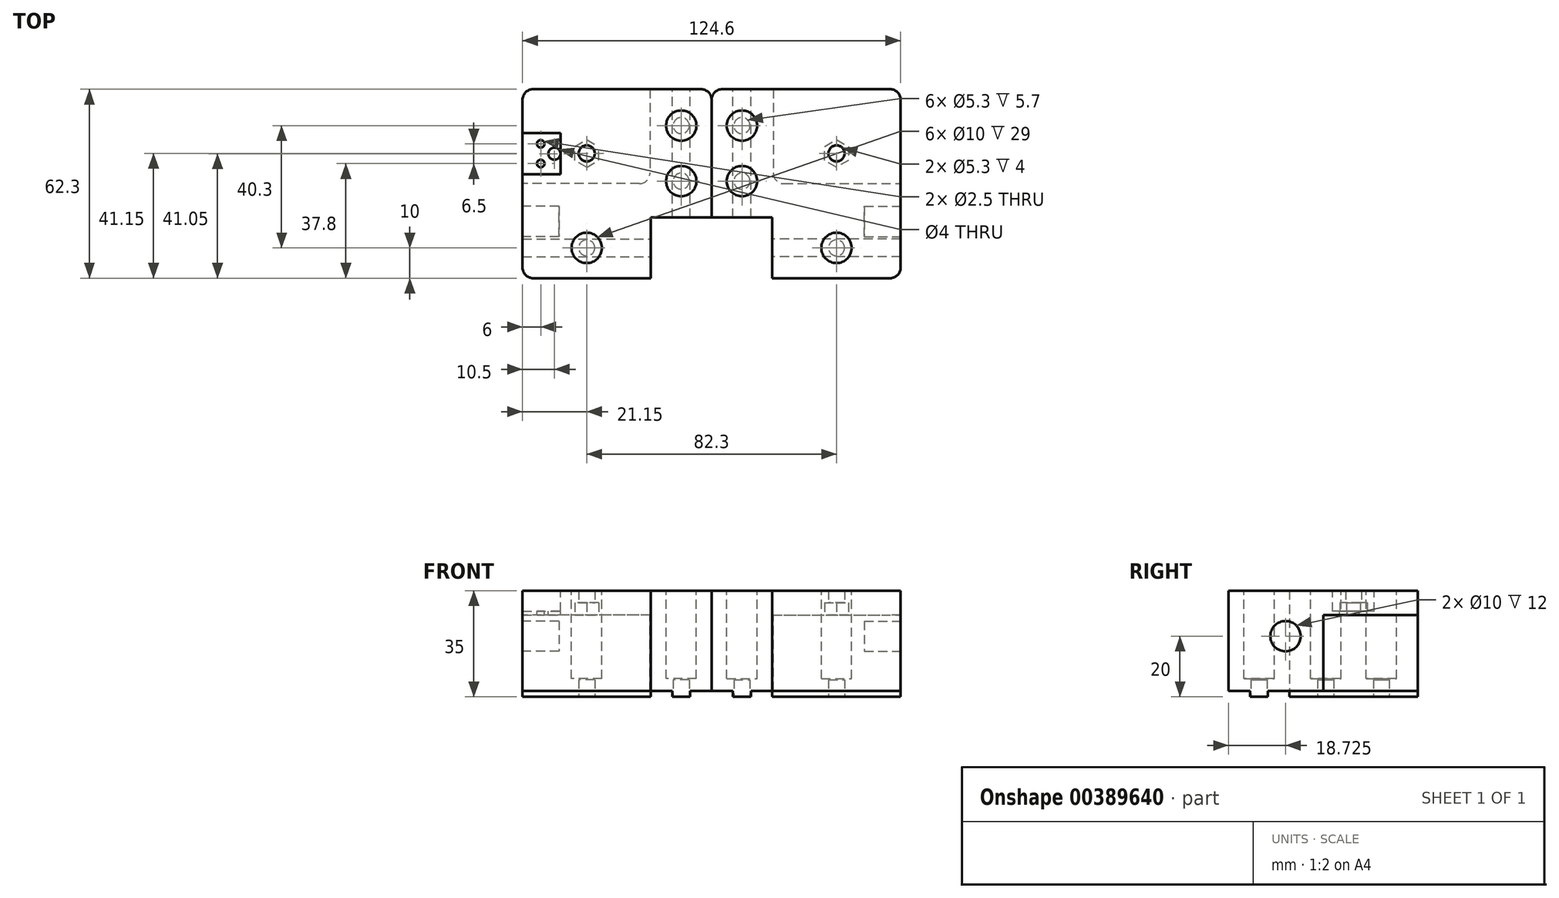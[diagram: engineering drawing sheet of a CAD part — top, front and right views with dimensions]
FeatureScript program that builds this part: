
annotation { "Feature Type Name" : "Feature", "Feature Type Description" : "" }
export const myFeature = defineFeature(function(context is Context, id is Id, definition is map)
    precondition{}
    {
        {
            var Q0;
            Q0=qCreatedBy(makeId("Top.planeOp"),FACE);
            var sketch = newSketch(context, id + "F0", { "sketchPlane" : qUnion([Q0])});
            skLineSegment(sketch, "E0.bottom", {"start": v(-21.15, 35) * mm, "end": v(41.15, 35) * mm});
            skLineSegment(sketch, "E0.top", {"start": v(-21.15, -27.3) * mm, "end": v(21.15, -27.3) * mm});
            skLineSegment(sketch, "E0.left", {"start": v(-21.15, 35) * mm, "end": v(-21.15, -27.3) * mm});
            skLineSegment(sketch, "E0.right", {"start": v(41.15, 35) * mm, "end": v(41.15, -7.3) * mm});
            skLineSegment(sketch, "E1.top", {"start": v(41.15, -7.3) * mm, "end": v(21.15, -7.3) * mm});
            skLineSegment(sketch, "E1.right", {"start": v(21.15, -27.3) * mm, "end": v(21.15, -7.3) * mm});
            skCircle(sketch, "E2", {"center": v(31.15, 23) * mm, "radius": 2.65 * mm});
            skCircle(sketch, "E3", {"center": v(31.15, 4.7) * mm, "radius": 2.65 * mm});
            skCircle(sketch, "E4", {"center": v(0, -17.3) * mm, "radius": 2.65 * mm});
            skPoint(sketch, "E4.centerSnap0", {"position": v(0, -27.3) * mm});
            skCircle(sketch, "E5", {"center": v(0, 13.85) * mm, "radius": 2.65 * mm});
            skSolve(sketch);
        }
        {
            var Q0;
            Q0=qSketchRegion(id+"F0",true);
            extrude(context, id + "F1", {"entities" : qUnion([Q0]), "depth" : 33 * mm});
        }
        {
            var Q0;
            Q0=makeQuery(id+"F1.opExtrude","SWEPT_FACE",FACE,{"disambiguationData":[OSD([sQuery(id+"F0.wireOp",EDGE,"E0.left")])]});
            var sketch = newSketch(context, id + "F2", { "sketchPlane" : qUnion([Q0])});
            skCircle(sketch, "E6", {"center": v(8.58, 18) * mm, "radius": 5 * mm});
            skSolve(sketch);
        }
        {
            var Q0;
            Q0=qSketchRegion(id+"F2",true);
            extrude(context, id + "F3", {"entities" : qUnion([Q0]), "operationType" : NewBodyOperationType.REMOVE, "oppositeDirection" : true, "depth" : 12 * mm});
        }
        {
            var Q0;
            Q0=makeQuery(id+"F1.opExtrude","CAP_FACE",FACE,{"disambiguationData":[OSD([sQuery(id+"F0.wireOp",EDGE,"E0.bottom"),sQuery(id+"F0.wireOp",EDGE,"E0.top"),sQuery(id+"F0.wireOp",EDGE,"E0.left"),sQuery(id+"F0.wireOp",EDGE,"E0.right"),sQuery(id+"F0.wireOp",EDGE,"E1.top"),sQuery(id+"F0.wireOp",EDGE,"E1.right"),sQuery(id+"F0.wireOp",EDGE,"E2"),sQuery(id+"F0.wireOp",EDGE,"E3"),sQuery(id+"F0.wireOp",EDGE,"YSbFCtBf-OZUa-blBg-jqSk-ddDIdjAn90QF"),sQuery(id+"F0.wireOp",EDGE,"E4"),sQuery(id+"F0.wireOp",EDGE,"E5")])],"isStart":true});
            var sketch = newSketch(context, id + "F4", { "sketchPlane" : qUnion([Q0])});
            skCircle(sketch, "E7.0", {"center": v(0, -13.85) * mm, "radius": 2.65 * mm, "construction": true});
            skCircle(sketch, "E8", {"center": v(0, -13.85) * mm, "radius": 3.95 * mm, "construction": true});
            skLineSegment(sketch, "E9", {"start": v(0, -20.58) * mm, "end": v(0, -4.16) * mm, "construction": true});
            skLineSegment(sketch, "E10", {"start": v(-6.74, -13.85) * mm, "end": v(6.1, -13.85) * mm, "construction": true});
            skLineSegment(sketch, "E11", {"start": v(-3.95, -16.13) * mm, "end": v(-3.95, -11.57) * mm});
            skLineSegment(sketch, "E12", {"start": v(-3.95, -11.57) * mm, "end": v(0, -9.29) * mm});
            skLineSegment(sketch, "E13", {"start": v(3.95, -16.13) * mm, "end": v(0, -18.41) * mm});
            skLineSegment(sketch, "E14", {"start": v(0, -18.41) * mm, "end": v(-3.95, -16.13) * mm});
            skLineSegment(sketch, "E15", {"start": v(3.95, -16.13) * mm, "end": v(3.95, -11.57) * mm});
            skLineSegment(sketch, "E16", {"start": v(3.95, -11.57) * mm, "end": v(0, -9.29) * mm});
            skSolve(sketch);
        }
        {
            var Q0;
            Q0=qSketchRegion(id+"F4",true);
            extrude(context, id + "F5", {"entities" : qUnion([Q0]), "operationType" : NewBodyOperationType.REMOVE, "oppositeDirection" : true, "depth" : 29 * mm});
        }
        {
            var Q0;
            Q0=makeQuery(id+"F1.opExtrude","CAP_FACE",FACE,{"disambiguationData":[OSD([sQuery(id+"F0.wireOp",EDGE,"E0.bottom"),sQuery(id+"F0.wireOp",EDGE,"E0.top"),sQuery(id+"F0.wireOp",EDGE,"E0.left"),sQuery(id+"F0.wireOp",EDGE,"E0.right"),sQuery(id+"F0.wireOp",EDGE,"E1.top"),sQuery(id+"F0.wireOp",EDGE,"E1.right"),sQuery(id+"F0.wireOp",EDGE,"E2"),sQuery(id+"F0.wireOp",EDGE,"E3"),sQuery(id+"F0.wireOp",EDGE,"YSbFCtBf-OZUa-blBg-jqSk-ddDIdjAn90QF"),sQuery(id+"F0.wireOp",EDGE,"E4"),sQuery(id+"F0.wireOp",EDGE,"E5")])],"isStart":false});
            var sketch = newSketch(context, id + "F6", { "sketchPlane" : qUnion([Q0])});
            skCircle(sketch, "E17.0", {"center": v(31.15, 23) * mm, "radius": 2.65 * mm, "construction": true});
            skCircle(sketch, "E18.0", {"center": v(31.15, 4.7) * mm, "radius": 2.65 * mm, "construction": true});
            skCircle(sketch, "E19.0", {"center": v(0, -17.3) * mm, "radius": 2.65 * mm, "construction": true});
            skCircle(sketch, "E20", {"center": v(31.15, 23) * mm, "radius": 5 * mm});
            skCircle(sketch, "E21", {"center": v(31.15, 4.7) * mm, "radius": 5 * mm});
            skCircle(sketch, "E22", {"center": v(0, -17.3) * mm, "radius": 5 * mm});
            skSolve(sketch);
        }
        {
            var Q0;
            Q0=qSketchRegion(id+"F6",true);
            extrude(context, id + "F7", {"entities" : qUnion([Q0]), "operationType" : NewBodyOperationType.REMOVE, "oppositeDirection" : true, "depth" : 29 * mm});
        }
        {
            var Q0;
            Q0=makeQuery(id+"F1.opExtrude","CAP_FACE",FACE,{"disambiguationData":[OSD([sQuery(id+"F0.wireOp",EDGE,"E0.bottom"),sQuery(id+"F0.wireOp",EDGE,"E0.top"),sQuery(id+"F0.wireOp",EDGE,"E0.left"),sQuery(id+"F0.wireOp",EDGE,"E0.right"),sQuery(id+"F0.wireOp",EDGE,"E1.top"),sQuery(id+"F0.wireOp",EDGE,"E1.right"),sQuery(id+"F0.wireOp",EDGE,"E2"),sQuery(id+"F0.wireOp",EDGE,"E3"),sQuery(id+"F0.wireOp",EDGE,"YSbFCtBf-OZUa-blBg-jqSk-ddDIdjAn90QF"),sQuery(id+"F0.wireOp",EDGE,"E4"),sQuery(id+"F0.wireOp",EDGE,"E5")])],"isStart":true});
            var sketch = newSketch(context, id + "F8", { "sketchPlane" : qUnion([Q0])});
            skLineSegment(sketch, "E23.bottom", {"start": v(28.2, 7.3) * mm, "end": v(34.1, 7.3) * mm});
            skLineSegment(sketch, "E23.top", {"start": v(28.2, -35) * mm, "end": v(34.1, -35) * mm});
            skLineSegment(sketch, "E23.left", {"start": v(28.2, 7.3) * mm, "end": v(28.2, -13.57) * mm});
            skLineSegment(sketch, "E23.right", {"start": v(34.1, 7.3) * mm, "end": v(34.1, -13.57) * mm});
            skCircle(sketch, "E24.0", {"center": v(31.15, -4.7) * mm, "radius": 2.65 * mm});
            skCircle(sketch, "E25.0", {"center": v(31.15, -23) * mm, "radius": 2.65 * mm});
            skLineSegment(sketch, "E26.trimOffspring", {"start": v(28.2, -13.57) * mm, "end": v(28.2, -35) * mm});
            skLineSegment(sketch, "E27.trimOffspring", {"start": v(34.1, -13.57) * mm, "end": v(34.1, -35) * mm});
            skLineSegment(sketch, "E28.bottom", {"start": v(-21.15, 20.25) * mm, "end": v(21.15, 20.25) * mm});
            skLineSegment(sketch, "E28.top", {"start": v(-21.15, 14.35) * mm, "end": v(21.15, 14.35) * mm});
            skLineSegment(sketch, "E28.left", {"start": v(-21.15, 20.25) * mm, "end": v(-21.15, 14.35) * mm});
            skLineSegment(sketch, "E28.right", {"start": v(21.15, 20.25) * mm, "end": v(21.15, 14.35) * mm});
            skCircle(sketch, "E29.0", {"center": v(0, 17.3) * mm, "radius": 2.65 * mm});
            skSolve(sketch);
        }
        {
            var Q0;
            Q0=qSketchRegion(id+"F8",true);
            extrude(context, id + "F9", {"entities" : qUnion([Q0]), "operationType" : NewBodyOperationType.ADD, "depth" : 2 * mm});
        }
        {
            var Q0;
            Q0=makeQuery(id+"F1.opExtrude","SWEPT_EDGE",EDGE,{"disambiguationData":[OSD([sQuery(id+"F0.wireOp",EDGE,"E0.top"),sQuery(id+"F0.wireOp",EDGE,"E0.left")])]});
            var Q1;
            Q1=makeQuery(id+"F1.opExtrude","SWEPT_EDGE",EDGE,{"disambiguationData":[OSD([sQuery(id+"F0.wireOp",EDGE,"E0.bottom"),sQuery(id+"F0.wireOp",EDGE,"E0.left")])]});
            var Q2;
            Q2=makeQuery(id+"F1.opExtrude","SWEPT_EDGE",EDGE,{"disambiguationData":[OSD([sQuery(id+"F0.wireOp",EDGE,"E0.bottom"),sQuery(id+"F0.wireOp",EDGE,"E0.right")])]});
            fillet(context, id + "F10", {"entities" : qUnion([Q0, Q1, Q2]), "radius" : 3.5 * mm, "tangentPropagation" : true, "allowEdgeOverflow" : false});
        }
        {
            var Q0;
            Q0=makeQuery(id+"F9.boolean.opBoolean","MERGE",FACE,{"derivedFrom":[makeQuery(id+"F1.opExtrude","SWEPT_FACE",FACE,{"disambiguationData":[OSD([sQuery(id+"F0.wireOp",EDGE,"E0.left")])]}),makeQuery(id+"F9.opExtrude","SWEPT_FACE",FACE,{"disambiguationData":[OSD([sQuery(id+"F8.wireOp",EDGE,"E28.left")])]})]});
            var sketch = newSketch(context, id + "F11", { "sketchPlane" : qUnion([Q0])});
            skPoint(sketch, "E30.oppositeSnap0", {"position": v(-3.85, 33) * mm});
            skLineSegment(sketch, "E30.bottom", {"start": v(-35, 0) * mm, "end": v(-3.85, 0) * mm});
            skLineSegment(sketch, "E30.top", {"start": v(-35, 25) * mm, "end": v(-3.85, 25) * mm});
            skLineSegment(sketch, "E30.left", {"start": v(-35, 0) * mm, "end": v(-35, 25) * mm});
            skLineSegment(sketch, "E30.right", {"start": v(-3.85, 0) * mm, "end": v(-3.85, 25) * mm});
            skSolve(sketch);
        }
        {
            var Q0;
            Q0=qSketchRegion(id+"F11",true);
            extrude(context, id + "F12", {"entities" : qUnion([Q0]), "operationType" : NewBodyOperationType.REMOVE, "oppositeDirection" : true, "depth" : 42 * mm});
        }
        {
            var Q0;
            Q0=makeQuery(id+"F12.boolean.opBoolean","COPY",EDGE,{"derivedFrom":makeQuery(id+"F12.opExtrude","CAP_EDGE",EDGE,{"disambiguationData":[OSD([sQuery(id+"F11.wireOp",EDGE,"E30.right")])],"isStart":true})});
            var Q1;
            Q1=makeQuery(id+"F12.boolean.opBoolean","COPY",EDGE,{"derivedFrom":makeQuery(id+"F12.opExtrude","CAP_EDGE",EDGE,{"disambiguationData":[OSD([sQuery(id+"F11.wireOp",EDGE,"E30.right")])],"isStart":false})});
            var Q2;
            Q2=makeQuery(id+"F12.boolean.opBoolean","COPY",EDGE,{"derivedFrom":makeQuery(id+"F12.opExtrude","CAP_EDGE",EDGE,{"disambiguationData":[OSD([sQuery(id+"F11.wireOp",EDGE,"E30.left")])],"isStart":false})});
            fillet(context, id + "F13", {"entities" : qUnion([Q0, Q1, Q2]), "radius" : 3.5 * mm, "tangentPropagation" : true, "allowEdgeOverflow" : false});
        }
        {
            var Q0;
            Q0=makeQuery(id+"F7.boolean.opBoolean","COPY",FACE,{"derivedFrom":makeQuery(id+"F7.opExtrude","CAP_FACE",FACE,{"disambiguationData":[OSD([sQuery(id+"F6.wireOp",EDGE,"E22")])],"isStart":false})});
            var sketch = newSketch(context, id + "F14", { "sketchPlane" : qUnion([Q0])});
            skCircle(sketch, "E31.0", {"center": v(0, -17.3) * mm, "radius": 2.65 * mm});
            skCircle(sketch, "E32.0", {"center": v(31.15, 4.7) * mm, "radius": 2.65 * mm});
            skCircle(sketch, "E33.0", {"center": v(31.15, 23) * mm, "radius": 2.65 * mm});
            skSolve(sketch);
        }
        {
            var Q0;
            Q0=qSketchRegion(id+"F14",true);
            extrude(context, id + "F15", {"entities" : qUnion([Q0]), "operationType" : NewBodyOperationType.ADD, "oppositeDirection" : true, "depth" : .3 * mm});
        }
        {
            var Q0;
            Q0=makeQuery(id+"F1.opExtrude","SWEPT_BODY",BODY,{"disambiguationData":[OSD([sQuery(id+"F0.wireOp",EDGE,"E0.bottom"),sQuery(id+"F0.wireOp",EDGE,"E0.top"),sQuery(id+"F0.wireOp",EDGE,"E0.left"),sQuery(id+"F0.wireOp",EDGE,"E0.right"),sQuery(id+"F0.wireOp",EDGE,"E1.top"),sQuery(id+"F0.wireOp",EDGE,"E1.right"),sQuery(id+"F0.wireOp",EDGE,"E2"),sQuery(id+"F0.wireOp",EDGE,"E3"),sQuery(id+"F0.wireOp",EDGE,"YSbFCtBf-OZUa-blBg-jqSk-ddDIdjAn90QF"),sQuery(id+"F0.wireOp",EDGE,"E4"),sQuery(id+"F0.wireOp",EDGE,"E5")])]});
            var Q1;
            Q1=makeQuery(id+"F1.opExtrude","SWEPT_FACE",FACE,{"disambiguationData":[OSD([sQuery(id+"F0.wireOp",EDGE,"E0.right")])]});
            mirror(context, id + "F16", {"entities" : qUnion([Q0]), "mirrorPlane" : qUnion([Q1])});
        }
        {
            var Q0;
            Q0=makeQuery(id+"F1.opExtrude","CAP_FACE",FACE,{"disambiguationData":[OSD([sQuery(id+"F0.wireOp",EDGE,"E0.bottom"),sQuery(id+"F0.wireOp",EDGE,"E0.top"),sQuery(id+"F0.wireOp",EDGE,"E0.left"),sQuery(id+"F0.wireOp",EDGE,"E0.right"),sQuery(id+"F0.wireOp",EDGE,"E1.top"),sQuery(id+"F0.wireOp",EDGE,"E1.right"),sQuery(id+"F0.wireOp",EDGE,"E2"),sQuery(id+"F0.wireOp",EDGE,"E3"),sQuery(id+"F0.wireOp",EDGE,"E4"),sQuery(id+"F0.wireOp",EDGE,"E5")])],"isStart":false});
            var sketch = newSketch(context, id + "F17", { "sketchPlane" : qUnion([Q0])});
            skLineSegment(sketch, "E34.bottom", {"start": v(-21.15, 20.6) * mm, "end": v(-13.65, 20.6) * mm});
            skLineSegment(sketch, "E34.top", {"start": v(-21.15, 6.9) * mm, "end": v(-13.65, 6.9) * mm});
            skLineSegment(sketch, "E34.left", {"start": v(-21.15, 20.6) * mm, "end": v(-21.15, 6.9) * mm});
            skLineSegment(sketch, "E34.right", {"start": v(-13.65, 20.6) * mm, "end": v(-13.65, 6.9) * mm});
            skLineSegment(sketch, "E35.bottom", {"start": v(-13.65, 20.6) * mm, "end": v(-8.65, 20.6) * mm});
            skLineSegment(sketch, "E35.top", {"start": v(-13.65, 6.9) * mm, "end": v(-8.65, 6.9) * mm});
            skLineSegment(sketch, "E35.left", {"start": v(-13.65, 20.6) * mm, "end": v(-13.65, 6.9) * mm, "construction": true});
            skLineSegment(sketch, "E35.right", {"start": v(-8.65, 20.6) * mm, "end": v(-8.65, 6.9) * mm});
            skSolve(sketch);
        }
        {
            var Q0;
            Q0=qSketchRegion(id+"F17",true);
            extrude(context, id + "F18", {"entities" : qUnion([Q0]), "operationType" : NewBodyOperationType.REMOVE, "oppositeDirection" : true, "depth" : 6.8 * mm});
        }
        {
            var Q0;
            Q0=makeQuery(id+"F18.boolean.opBoolean","COPY",FACE,{"derivedFrom":makeQuery(id+"F18.opExtrude","CAP_FACE",FACE,{"disambiguationData":[OSD([sQuery(id+"F17.wireOp",EDGE,"E34.bottom"),sQuery(id+"F17.wireOp",EDGE,"E34.top"),sQuery(id+"F17.wireOp",EDGE,"E34.left"),sQuery(id+"F17.wireOp",EDGE,"E34.right")])],"isStart":false})});
            var sketch = newSketch(context, id + "F19", { "sketchPlane" : qUnion([Q0])});
            skCircle(sketch, "E36", {"center": v(-15.15, 17) * mm, "radius": 1.25 * mm});
            skCircle(sketch, "E37", {"center": v(-15.15, 10.5) * mm, "radius": 1.25 * mm});
            skSolve(sketch);
        }
        {
            var Q0;
            Q0=qSketchRegion(id+"F19",true);
            extrude(context, id + "F20", {"entities" : qUnion([Q0]), "operationType" : NewBodyOperationType.REMOVE, "oppositeDirection" : true, "depth" : 8 * mm});
        }
        {
            var Q0;
            Q0=makeQuery(id+"F18.boolean.opBoolean","COPY",FACE,{"derivedFrom":makeQuery(id+"F18.opExtrude","CAP_FACE",FACE,{"disambiguationData":[OSD([sQuery(id+"F17.wireOp",EDGE,"E34.bottom"),sQuery(id+"F17.wireOp",EDGE,"E34.top"),sQuery(id+"F17.wireOp",EDGE,"E34.left"),sQuery(id+"F17.wireOp",EDGE,"E35.bottom"),sQuery(id+"F17.wireOp",EDGE,"E35.top"),sQuery(id+"F17.wireOp",EDGE,"E35.right")])],"isStart":false})});
            var sketch = newSketch(context, id + "F21", { "sketchPlane" : qUnion([Q0])});
            skCircle(sketch, "E38", {"center": v(-10.65, 13.75) * mm, "radius": 2 * mm});
            skPoint(sketch, "E38.centerSnap0", {"position": v(-8.65, 13.75) * mm});
            skSolve(sketch);
        }
        {
            var Q0;
            Q0=qSketchRegion(id+"F21",true);
            extrude(context, id + "F22", {"entities" : qUnion([Q0]), "operationType" : NewBodyOperationType.REMOVE, "oppositeDirection" : true, "depth" : 30 * mm});
        }
    });
